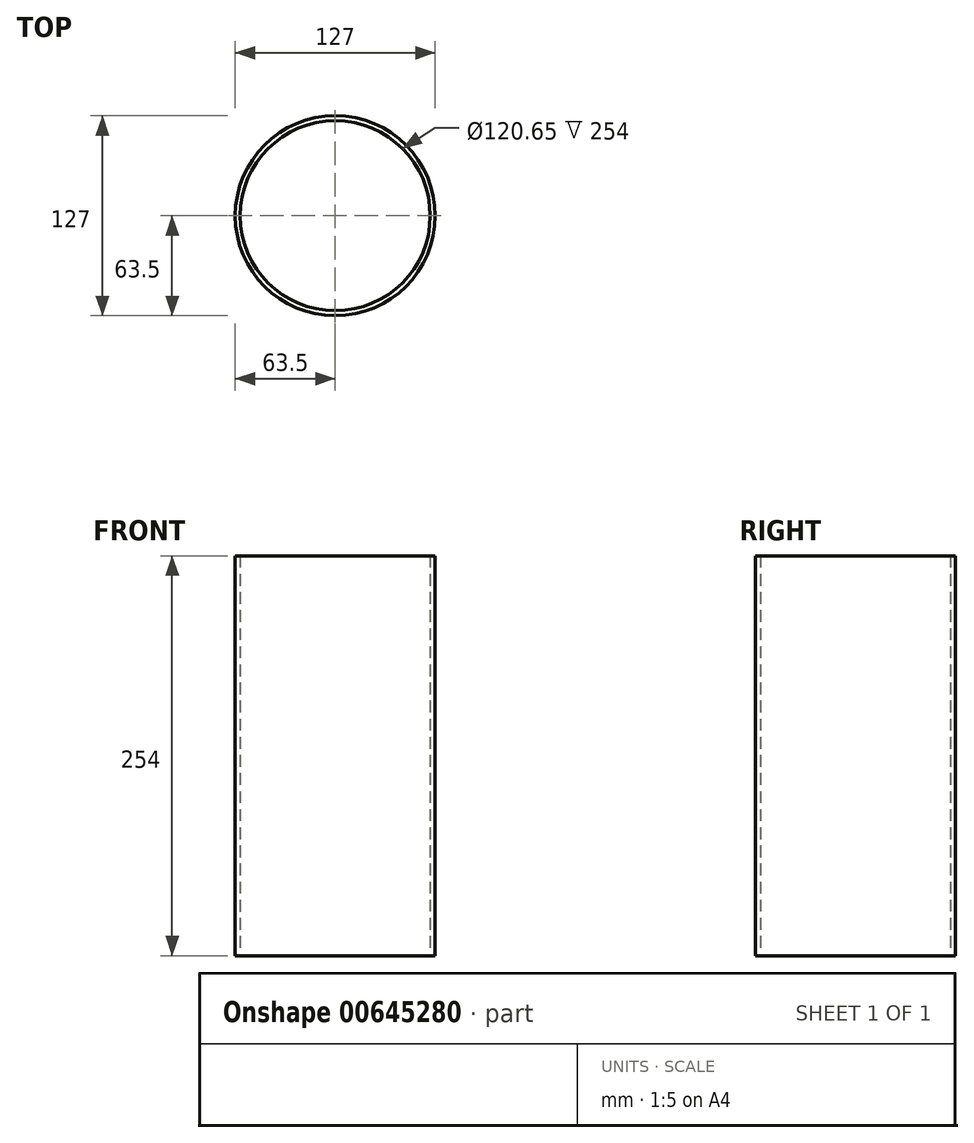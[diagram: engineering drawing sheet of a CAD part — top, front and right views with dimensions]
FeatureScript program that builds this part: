
annotation { "Feature Type Name" : "Feature", "Feature Type Description" : "" }
export const myFeature = defineFeature(function(context is Context, id is Id, definition is map)
    precondition{}
    {
        {
            var Q0;
            Q0=qCreatedBy(makeId("Top.planeOp"),FACE);
            var sketch = newSketch(context, id + "F0", { "sketchPlane" : qUnion([Q0])});
            skCircle(sketch, "E0", {"center": v(0, 0) * mm, "radius": 63.5 * mm});
            skSolve(sketch);
        }
        {
            var Q0;
            Q0 = qSketchRegion(id + "F0", true);
            var Q1;
            Q1 = qSketchRegion(id + "F2", true);
            extrude(context, id + "F1", {"entities" : qUnion([Q0, Q1]), "depth" : 254 * mm, "offsetDistance" : 25.4 * mm});
        }
        {
            var Q0;
            Q0=qCreatedBy(makeId("Top.planeOp"),FACE);
            var sketch = newSketch(context, id + "F2", { "sketchPlane" : qUnion([Q0])});
            skPoint(sketch, "E1", {"position": v(0, 0) * mm});
            skSolve(sketch);
        }
        {
            var Q0;
            Q0=sQuery(id+"F2.wireOp",VERTEX,"E1");
            var Q1;
            Q1=makeQuery(id+"F1.opExtrude","SWEPT_BODY",BODY,{"disambiguationData":[OSD([sQuery(id+"F0.wireOp",EDGE,"E0")])]});
            hole(context, id + "F3", {"style" : HoleStyle.SIMPLE, "endStyle" : HoleEndStyle.THROUGH, "oppositeDirection" : true, "holeDiameter" : 120.65 * mm, "majorDiameter" : 6.35 * mm, "isTappedThrough" : true, "tappedDepth" : 12.7 * mm, "tapClearance" : 3, "locations" : qUnion([Q0]), "scope" : qUnion([Q1])});
        }
    });
